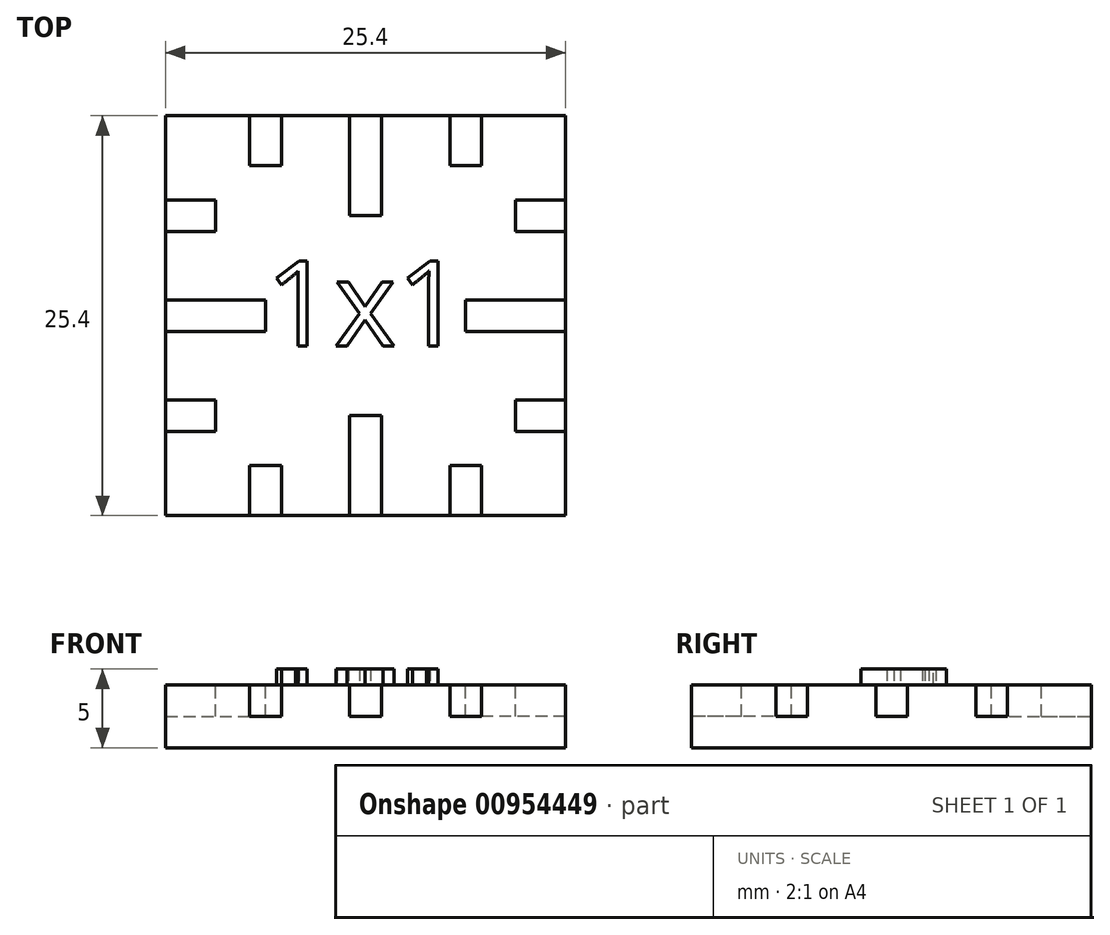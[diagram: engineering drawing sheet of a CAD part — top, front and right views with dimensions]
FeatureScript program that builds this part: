
annotation { "Feature Type Name" : "Feature", "Feature Type Description" : "" }
export const myFeature = defineFeature(function(context is Context, id is Id, definition is map)
    precondition{}
    {
        {
            var Q0;
            Q0=qCreatedBy(makeId("Top.planeOp"),FACE);
            var sketch = newSketch(context, id + "F0", { "sketchPlane" : qUnion([Q0])});
            skLineSegment(sketch, "E0.bottom", {"start": v(-12.7, 12.7) * mm, "end": v(12.7, 12.7) * mm});
            skLineSegment(sketch, "E0.top", {"start": v(-12.7, -12.7) * mm, "end": v(12.7, -12.7) * mm});
            skLineSegment(sketch, "E0.left", {"start": v(-12.7, 12.7) * mm, "end": v(-12.7, -12.7) * mm});
            skLineSegment(sketch, "E0.right", {"start": v(12.7, 12.7) * mm, "end": v(12.7, -12.7) * mm});
            skPoint(sketch, "E0.middle", {"position": v(0, 0) * mm});
            skSolve(sketch);
        }
        {
            var Q0;
            Q0=makeQuery(id+"F0.imprint","IMPRINT",FACE,{"disambiguationData":[TD([[makeQuery(id+"F0.imprint","IMPRINT",EDGE,{"derivedFrom":sQuery(id+"F0.wireOp",EDGE,"E0.bottom")}),-1.0]])]});
            extrude(context, id + "F1", {"entities" : qUnion([Q0]), "depth" : 4 * mm, "offsetDistance" : 25 * mm});
        }
        {
            var Q0;
            Q0=makeQuery(id+"F1.opExtrude","CAP_FACE",FACE,{"disambiguationData":[OSD([sQuery(id+"F0.wireOp",EDGE,"E0.bottom"),sQuery(id+"F0.wireOp",EDGE,"E0.top"),sQuery(id+"F0.wireOp",EDGE,"E0.left"),sQuery(id+"F0.wireOp",EDGE,"E0.right")])],"isStart":false});
            var sketch = newSketch(context, id + "F2", { "sketchPlane" : qUnion([Q0])});
            skLineSegment(sketch, "E1.bottom", {"start": v(-1, -6.35) * mm, "end": v(1, -6.35) * mm});
            skLineSegment(sketch, "E1.top", {"start": v(-1, -19.05) * mm, "end": v(1, -19.05) * mm});
            skLineSegment(sketch, "E1.left", {"start": v(-1, -6.35) * mm, "end": v(-1, -19.05) * mm});
            skLineSegment(sketch, "E1.right", {"start": v(1, -6.35) * mm, "end": v(1, -19.05) * mm});
            skPoint(sketch, "E1.middle", {"position": v(0, -12.7) * mm});
            skLineSegment(sketch, "E2.bottom", {"start": v(5.35, -9.53) * mm, "end": v(7.35, -9.53) * mm});
            skLineSegment(sketch, "E2.top", {"start": v(5.35, -15.88) * mm, "end": v(7.35, -15.88) * mm});
            skLineSegment(sketch, "E2.left", {"start": v(5.35, -9.53) * mm, "end": v(5.35, -15.88) * mm});
            skLineSegment(sketch, "E2.right", {"start": v(7.35, -9.53) * mm, "end": v(7.35, -15.88) * mm});
            skPoint(sketch, "E2.middle", {"position": v(6.35, -12.7) * mm});
            skLineSegment(sketch, "E3.bottom", {"start": v(-7.35, -9.53) * mm, "end": v(-5.35, -9.53) * mm});
            skLineSegment(sketch, "E3.top", {"start": v(-7.35, -15.88) * mm, "end": v(-5.35, -15.88) * mm});
            skLineSegment(sketch, "E3.left", {"start": v(-7.35, -9.53) * mm, "end": v(-7.35, -15.88) * mm});
            skLineSegment(sketch, "E3.right", {"start": v(-5.35, -9.53) * mm, "end": v(-5.35, -15.88) * mm});
            skPoint(sketch, "E3.middle", {"position": v(-6.35, -12.7) * mm});
            skLineSegment(sketch, "E4.bottom", {"start": v(-19.05, -1) * mm, "end": v(-19.05, 1) * mm});
            skLineSegment(sketch, "E4.top", {"start": v(-6.35, -1) * mm, "end": v(-6.35, 1) * mm});
            skLineSegment(sketch, "E4.left", {"start": v(-19.05, -1) * mm, "end": v(-6.35, -1) * mm});
            skLineSegment(sketch, "E4.right", {"start": v(-19.05, 1) * mm, "end": v(-6.35, 1) * mm});
            skPoint(sketch, "E4.middle", {"position": v(-12.7, 0) * mm});
            skLineSegment(sketch, "E5.bottom", {"start": v(-15.88, 5.35) * mm, "end": v(-15.88, 7.35) * mm});
            skLineSegment(sketch, "E5.top", {"start": v(-9.53, 5.35) * mm, "end": v(-9.53, 7.35) * mm});
            skLineSegment(sketch, "E5.left", {"start": v(-15.88, 5.35) * mm, "end": v(-9.53, 5.35) * mm});
            skLineSegment(sketch, "E5.right", {"start": v(-15.88, 7.35) * mm, "end": v(-9.53, 7.35) * mm});
            skPoint(sketch, "E5.middle", {"position": v(-12.7, 6.35) * mm});
            skLineSegment(sketch, "E6.bottom", {"start": v(-15.88, -7.35) * mm, "end": v(-15.88, -5.35) * mm});
            skLineSegment(sketch, "E6.top", {"start": v(-9.53, -7.35) * mm, "end": v(-9.53, -5.35) * mm});
            skLineSegment(sketch, "E6.left", {"start": v(-15.88, -7.35) * mm, "end": v(-9.52, -7.35) * mm});
            skLineSegment(sketch, "E6.right", {"start": v(-15.88, -5.35) * mm, "end": v(-9.52, -5.35) * mm});
            skPoint(sketch, "E6.middle", {"position": v(-12.7, -6.35) * mm});
            skLineSegment(sketch, "E7.bottom", {"start": v(1, 6.35) * mm, "end": v(-1, 6.35) * mm});
            skLineSegment(sketch, "E7.top", {"start": v(1, 19.05) * mm, "end": v(-1, 19.05) * mm});
            skLineSegment(sketch, "E7.left", {"start": v(1, 6.35) * mm, "end": v(1, 19.05) * mm});
            skLineSegment(sketch, "E7.right", {"start": v(-1, 6.35) * mm, "end": v(-1, 19.05) * mm});
            skPoint(sketch, "E7.middle", {"position": v(0, 12.7) * mm});
            skLineSegment(sketch, "E8.bottom", {"start": v(-5.35, 9.53) * mm, "end": v(-7.35, 9.53) * mm});
            skLineSegment(sketch, "E8.top", {"start": v(-5.35, 15.88) * mm, "end": v(-7.35, 15.88) * mm});
            skLineSegment(sketch, "E8.left", {"start": v(-5.35, 9.53) * mm, "end": v(-5.35, 15.88) * mm});
            skLineSegment(sketch, "E8.right", {"start": v(-7.35, 9.53) * mm, "end": v(-7.35, 15.88) * mm});
            skPoint(sketch, "E8.middle", {"position": v(-6.35, 12.7) * mm});
            skLineSegment(sketch, "E9.bottom", {"start": v(7.35, 9.52) * mm, "end": v(5.35, 9.52) * mm});
            skLineSegment(sketch, "E9.top", {"start": v(7.35, 15.88) * mm, "end": v(5.35, 15.88) * mm});
            skLineSegment(sketch, "E9.left", {"start": v(7.35, 9.52) * mm, "end": v(7.35, 15.88) * mm});
            skLineSegment(sketch, "E9.right", {"start": v(5.35, 9.52) * mm, "end": v(5.35, 15.88) * mm});
            skPoint(sketch, "E9.middle", {"position": v(6.35, 12.7) * mm});
            skLineSegment(sketch, "E10.bottom", {"start": v(19.05, 1) * mm, "end": v(19.05, -1) * mm});
            skLineSegment(sketch, "E10.top", {"start": v(6.35, 1) * mm, "end": v(6.35, -1) * mm});
            skLineSegment(sketch, "E10.left", {"start": v(19.05, 1) * mm, "end": v(6.35, 1) * mm});
            skLineSegment(sketch, "E10.right", {"start": v(19.05, -1) * mm, "end": v(6.35, -1) * mm});
            skPoint(sketch, "E10.middle", {"position": v(12.7, 0) * mm});
            skLineSegment(sketch, "E11.bottom", {"start": v(15.88, -5.35) * mm, "end": v(15.88, -7.35) * mm});
            skLineSegment(sketch, "E11.top", {"start": v(9.52, -5.35) * mm, "end": v(9.52, -7.35) * mm});
            skLineSegment(sketch, "E11.left", {"start": v(15.88, -5.35) * mm, "end": v(9.52, -5.35) * mm});
            skLineSegment(sketch, "E11.right", {"start": v(15.88, -7.35) * mm, "end": v(9.52, -7.35) * mm});
            skPoint(sketch, "E11.middle", {"position": v(12.7, -6.35) * mm});
            skLineSegment(sketch, "E12.bottom", {"start": v(15.88, 7.35) * mm, "end": v(15.88, 5.35) * mm});
            skLineSegment(sketch, "E12.top", {"start": v(9.53, 7.35) * mm, "end": v(9.53, 5.35) * mm});
            skLineSegment(sketch, "E12.left", {"start": v(15.88, 7.35) * mm, "end": v(9.52, 7.35) * mm});
            skLineSegment(sketch, "E12.right", {"start": v(15.88, 5.35) * mm, "end": v(9.52, 5.35) * mm});
            skPoint(sketch, "E12.middle", {"position": v(12.7, 6.35) * mm});
            skSolve(sketch);
        }
        {
            var Q0;
            Q0 = qSketchRegion(id + "F2", true);
            extrude(context, id + "F3", {"entities" : qUnion([Q0]), "operationType" : NewBodyOperationType.REMOVE, "oppositeDirection" : true, "depth" : 2 * mm, "offsetDistance" : 25 * mm});
        }
        {
            var Q0;
            Q0=makeQuery(id+"F1.opExtrude","CAP_FACE",FACE,{"disambiguationData":[OSD([sQuery(id+"F0.wireOp",EDGE,"E0.bottom"),sQuery(id+"F0.wireOp",EDGE,"E0.top"),sQuery(id+"F0.wireOp",EDGE,"E0.left"),sQuery(id+"F0.wireOp",EDGE,"E0.right")])],"isStart":false});
            var sketch = newSketch(context, id + "F4", { "sketchPlane" : qUnion([Q0])});
            skText(sketch, "E13", { "text": "1x1", "fontName": "OpenSans-Regular.ttf"});
            const initialGuessF4  = {"E13": [-0.00635, -0.00193, 1, 0, 0.00546]};
            skSetInitialGuess(sketch, initialGuessF4);
            skSolve(sketch);
        }
        {
            var Q0;
            Q0 = qSketchRegion(id + "F4", true);
            extrude(context, id + "F5", {"entities" : qUnion([Q0]), "operationType" : NewBodyOperationType.ADD, "depth" : 1 * mm, "offsetDistance" : 25 * mm});
        }
    });
